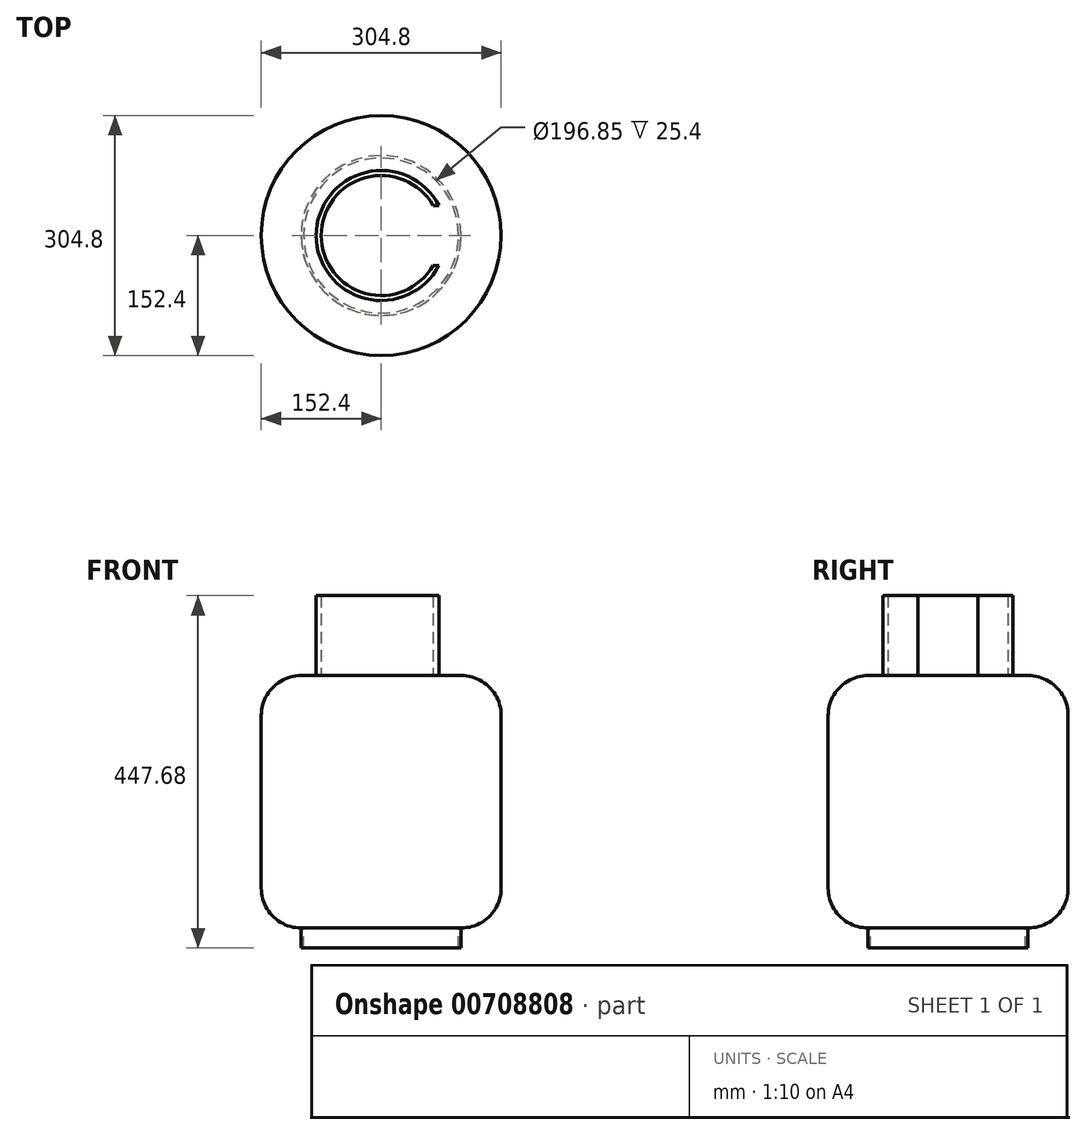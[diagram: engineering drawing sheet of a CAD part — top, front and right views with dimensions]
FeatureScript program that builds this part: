
annotation { "Feature Type Name" : "Feature", "Feature Type Description" : "" }
export const myFeature = defineFeature(function(context is Context, id is Id, definition is map)
    precondition{}
    {
        {
            var Q0;
            Q0=qCreatedBy(makeId("Top.planeOp"),FACE);
            var sketch = newSketch(context, id + "F0", { "sketchPlane" : qUnion([Q0])});
            skCircle(sketch, "E0", {"center": v(0, 0) * mm, "radius": 152.4 * mm});
            skSolve(sketch);
        }
        {
            var Q0;
            Q0 = qSketchRegion(id + "F0", true);
            extrude(context, id + "F1", {"entities" : qUnion([Q0]), "depth" : 320.67 * mm, "offsetDistance" : 25.4 * mm});
        }
        {
            var Q0;
            Q0=makeQuery(id+"F1.opExtrude","CAP_FACE",FACE,{"disambiguationData":[OSD([sQuery(id+"F0.wireOp",EDGE,"E0")])],"isStart":false});
            var sketch = newSketch(context, id + "F2", { "sketchPlane" : qUnion([Q0])});
            skCircle(sketch, "E1", {"center": v(0, 0) * mm, "radius": 82.55 * mm});
            skCircle(sketch, "E2.0", {"center": v(0, 0) * mm, "radius": 76.2 * mm});
            skSolve(sketch);
        }
        {
            var Q0;
            Q0 = qSketchRegion(id + "F2", true);
            extrude(context, id + "F3", {"entities" : qUnion([Q0]), "operationType" : NewBodyOperationType.ADD, "depth" : 101.6 * mm, "offsetDistance" : 25.4 * mm});
        }
        {
            var Q0;
            Q0=makeQuery(id+"F1.opExtrude","CAP_FACE",FACE,{"disambiguationData":[OSD([sQuery(id+"F0.wireOp",EDGE,"E0")])],"isStart":true});
            var sketch = newSketch(context, id + "F4", { "sketchPlane" : qUnion([Q0])});
            skCircle(sketch, "E3", {"center": v(0, 0) * mm, "radius": 101.6 * mm});
            skCircle(sketch, "E4.0", {"center": v(0, 0) * mm, "radius": 98.43 * mm});
            skSolve(sketch);
        }
        {
            var Q0;
            Q0 = qSketchRegion(id + "F4", true);
            extrude(context, id + "F5", {"entities" : qUnion([Q0]), "operationType" : NewBodyOperationType.ADD, "depth" : 25.4 * mm, "offsetDistance" : 25.4 * mm});
        }
        {
            var Q0;
            Q0=makeQuery(id+"F1.opExtrude","CAP_EDGE",EDGE,{"disambiguationData":[OSD([sQuery(id+"F0.wireOp",EDGE,"E0")])],"isStart":true});
            var Q1;
            Q1=makeQuery(id+"F1.opExtrude","CAP_EDGE",EDGE,{"disambiguationData":[OSD([sQuery(id+"F0.wireOp",EDGE,"E0")])],"isStart":false});
            fillet(context, id + "F6", {"entities" : qUnion([Q0, Q1]), "radius" : 50.8 * mm, "tangentPropagation" : true, "allowEdgeOverflow" : false});
        }
        {
            var Q0;
            Q0=qCreatedBy(makeId("Right.planeOp"),FACE);
            var sketch = newSketch(context, id + "F7", { "sketchPlane" : qUnion([Q0])});
            skLineSegment(sketch, "E5.bottom", {"start": v(-38.1, 422.28) * mm, "end": v(38.1, 422.28) * mm});
            skLineSegment(sketch, "E5.top", {"start": v(-38.1, 320.68) * mm, "end": v(38.1, 320.68) * mm});
            skLineSegment(sketch, "E5.left", {"start": v(-38.1, 422.28) * mm, "end": v(-38.1, 320.68) * mm});
            skLineSegment(sketch, "E5.right", {"start": v(38.1, 422.28) * mm, "end": v(38.1, 320.68) * mm});
            skLineSegment(sketch, "E6", {"start": v(0, 422.28) * mm, "end": v(0, 379.94) * mm, "construction": true});
            skSolve(sketch);
        }
        {
            var Q0;
            Q0 = qSketchRegion(id + "F7", true);
            var Q1;
            Q1=makeQuery(id+"F3.opExtrude","SWEPT_FACE",FACE,{"disambiguationData":[OSD([sQuery(id+"F2.wireOp",EDGE,"E1")])]});
            extrude(context, id + "F8", {"entities" : qUnion([Q0]), "operationType" : NewBodyOperationType.REMOVE, "endBound" : BoundingType.UP_TO_SURFACE, "depth" : 25.4 * mm, "endBoundEntityFace" : qUnion([Q1]), "offsetDistance" : 25.4 * mm});
        }
    });
